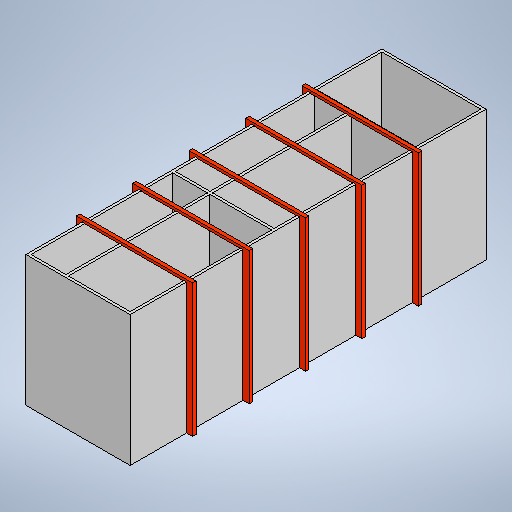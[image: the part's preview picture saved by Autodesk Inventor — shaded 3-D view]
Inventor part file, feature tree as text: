
AUTODESK INVENTOR PART (.ipt)
format: ipt  version: 2025.1 (Build 291241020, 241B)  size: 356,352 bytes
history: native  units: mm
features: extrude x5, sketch x5, projected_geometry x5, pattern_linear x1
ambient origin geometry x8: Origin, YZ Plane, XZ Plane, XY Plane, X Axis, Y Axis, Z Axis, Center Point
bodies: Solid1 (feature_tree)
feature tree (16):
  extrude  "Extrusion1"  Depth=8200.0mm
  extrude  "Extrusion2"  Depth=60.0mm
  sketch  "Sketch5"  dims[d11=140.0mm d12=80.0mm d13=1620.0mm d14=3000.0mm d15=0.0mm d16=50.0mm d18=1300.0mm d19=60.0mm d20=0.0mm d21=76.0mm d23=1300.0mm d24=350.0mm d25=90.0mm d26=150.0mm d27=1400.0mm d28=750.0mm d29=90.0mm d30=3500.0mm d31=620.0mm d32=1650.0mm d33=100.0mm d34=0.0mm]
  extrude  "Extrusion3"  Depth=1500.0mm
  extrude  "Extrusion4"  Depth=3200.0mm
  pattern_linear  "Rectangular Pattern1"  Count1=300 Spacing1=0.0mm
  extrude  "Extrusion5"  Depth=80.0mm
  sketch  "Sketch1"  dims[d0=2400.0mm d1=8200.0mm]
  sketch  "Sketch2"  dims[d2=10.0mm d3=0.0mm d4=60.0mm]
  projected_geometry  "Projected Loop1"
  sketch  "Sketch3"  dims[d5=60.0mm d6=1500.0mm]
  projected_geometry  "Projected Loop2"
  sketch  "Sketch4"  dims[d7=800.0mm d8=3200.0mm d9=3000.0mm d10=0.0mm]
  projected_geometry  "Projected Loop3"
  projected_geometry  "Projected Loop4"
  projected_geometry  "Projected Loop5"
